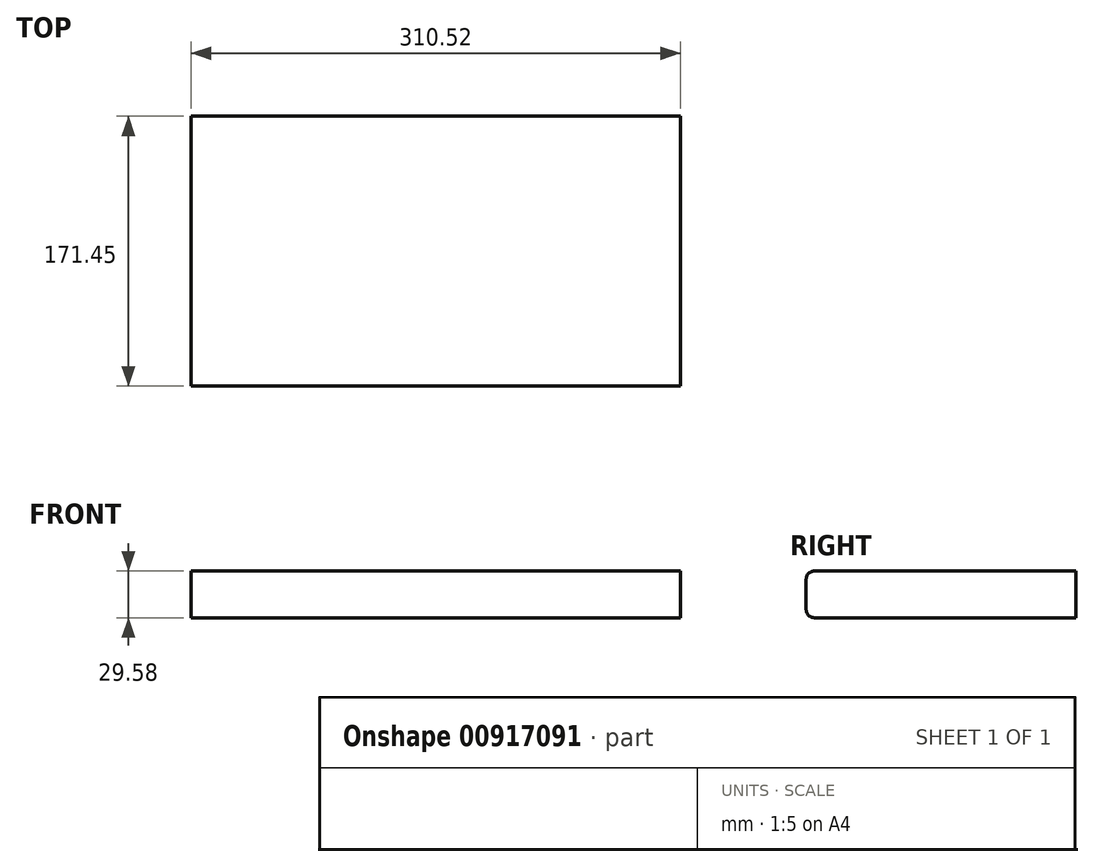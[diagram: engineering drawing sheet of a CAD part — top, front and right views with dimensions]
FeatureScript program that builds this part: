
annotation { "Feature Type Name" : "Feature", "Feature Type Description" : "" }
export const myFeature = defineFeature(function(context is Context, id is Id, definition is map)
    precondition{}
    {
        {
            var Q0;
            Q0=qCreatedBy(makeId("Front.planeOp"),FACE);
            var sketch = newSketch(context, id + "F0", { "sketchPlane" : qUnion([Q0])});
            skLineSegment(sketch, "E0.bottom", {"start": v(-156.38, 29.58) * mm, "end": v(154.14, 29.58) * mm});
            skLineSegment(sketch, "E0.top", {"start": v(-156.38, 0) * mm, "end": v(154.14, 0) * mm});
            skLineSegment(sketch, "E0.left", {"start": v(-156.38, 29.58) * mm, "end": v(-156.38, 0) * mm});
            skLineSegment(sketch, "E0.right", {"start": v(154.14, 29.58) * mm, "end": v(154.14, 0) * mm});
            skSolve(sketch);
        }
        {
            var Q0;
            Q0=makeQuery(id+"F0.imprint","IMPRINT",FACE,{"disambiguationData":[TD([[makeQuery(id+"F0.imprint","IMPRINT",EDGE,{"derivedFrom":sQuery(id+"F0.wireOp",EDGE,"E0.bottom")}),-1.0]])]});
            extrude(context, id + "F1", {"entities" : qUnion([Q0]), "depth" : 85.1 * mm, "offsetDistance" : 25.4 * mm});
        }
        {
            var Q0;
            Q0=makeQuery(id+"F1.opExtrude","CAP_FACE",FACE,{"disambiguationData":[OSD([sQuery(id+"F0.wireOp",EDGE,"E0.bottom"),sQuery(id+"F0.wireOp",EDGE,"E0.top"),sQuery(id+"F0.wireOp",EDGE,"E0.left"),sQuery(id+"F0.wireOp",EDGE,"E0.right")])],"isStart":true});
            extrude(context, id + "F2", {"entities" : qUnion([Q0]), "operationType" : NewBodyOperationType.ADD, "depth" : 86.36 * mm, "offsetDistance" : 25.4 * mm});
        }
        {
            var Q0;
            Q0=makeQuery(id+"F1.opExtrude","CAP_EDGE",EDGE,{"disambiguationData":[OSD([sQuery(id+"F0.wireOp",EDGE,"E0.bottom")])],"isStart":false});
            fillet(context, id + "F3", {"entities" : qUnion([Q0]), "radius" : 5.08 * mm, "tangentPropagation" : true, "allowEdgeOverflow" : false});
        }
        {
            var Q0;
            Q0=makeQuery(id+"F1.opExtrude","CAP_EDGE",EDGE,{"disambiguationData":[OSD([sQuery(id+"F0.wireOp",EDGE,"E0.top")])],"isStart":false});
            fillet(context, id + "F4", {"entities" : qUnion([Q0]), "radius" : 5.08 * mm, "tangentPropagation" : true, "allowEdgeOverflow" : false});
        }
        {
            var Q0;
            Q0=makeQuery(id+"F1.opExtrude","CAP_FACE",FACE,{"disambiguationData":[OSD([sQuery(id+"F0.wireOp",EDGE,"E0.bottom"),sQuery(id+"F0.wireOp",EDGE,"E0.top"),sQuery(id+"F0.wireOp",EDGE,"E0.left"),sQuery(id+"F0.wireOp",EDGE,"E0.right")])],"isStart":false});
            cPlane(context, id + "F5", {"entities" : qUnion([Q0]), "cplaneType" : CPlaneType.OFFSET, "offset" : 25.4 * mm, "width" : 152.4 * mm, "height" : 152.4 * mm});
        }
    });
